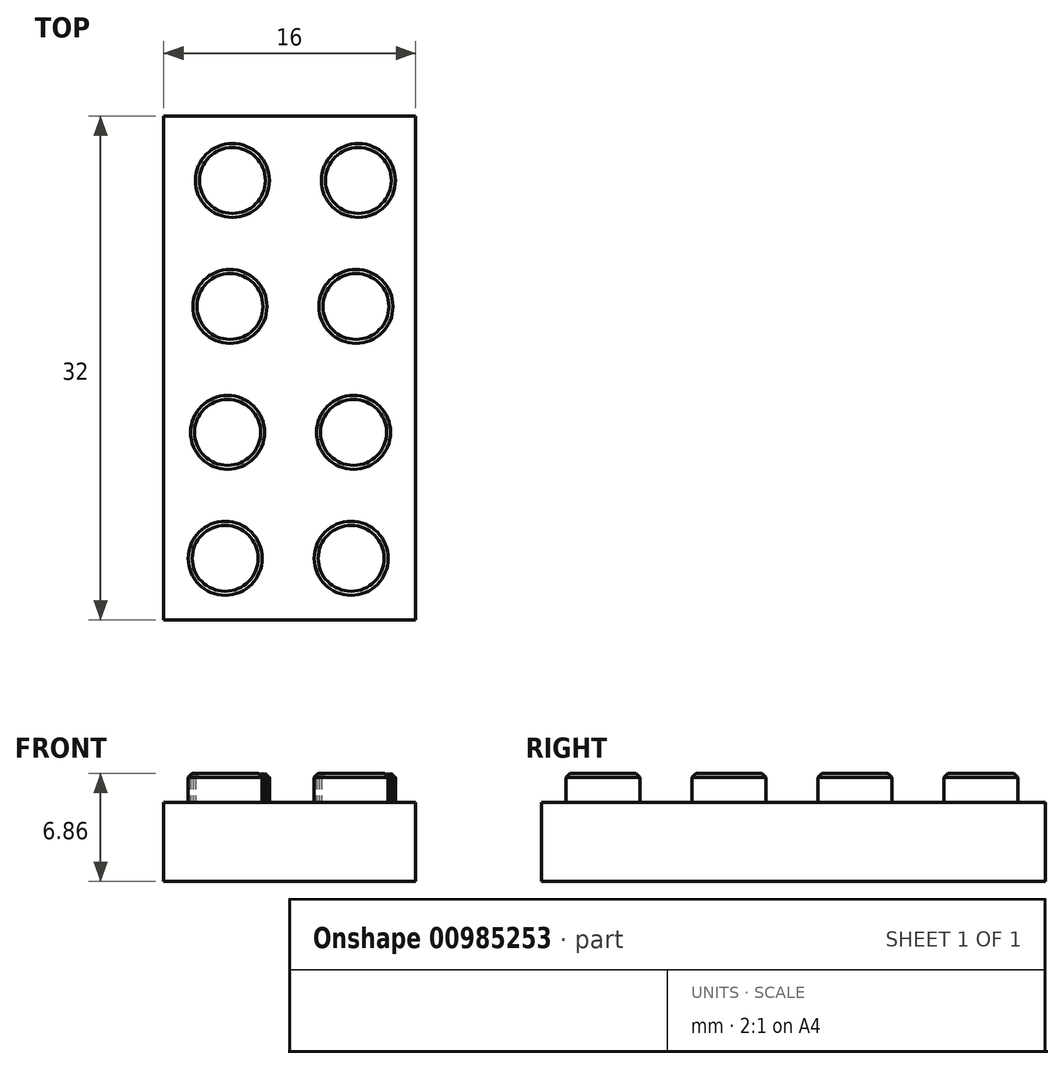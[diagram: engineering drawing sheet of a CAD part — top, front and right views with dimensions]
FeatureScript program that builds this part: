
annotation { "Feature Type Name" : "Feature", "Feature Type Description" : "" }
export const myFeature = defineFeature(function(context is Context, id is Id, definition is map)
    precondition{}
    {
        {
            var Q0;
            Q0=qCreatedBy(makeId("Top.planeOp"),FACE);
            var sketch = newSketch(context, id + "F0", { "sketchPlane" : qUnion([Q0])});
            skLineSegment(sketch, "E0.bottom", {"start": v(0, 0) * mm, "end": v(-16, 0) * mm});
            skLineSegment(sketch, "E0.top", {"start": v(0, 32) * mm, "end": v(-16, 32) * mm});
            skLineSegment(sketch, "E0.left", {"start": v(0, 0) * mm, "end": v(0, 32) * mm});
            skLineSegment(sketch, "E0.right", {"start": v(-16, 0) * mm, "end": v(-16, 32) * mm});
            skSolve(sketch);
        }
        {
            var Q0;
            Q0=makeQuery(id+"F0.imprint","IMPRINT",FACE,{"disambiguationData":[TD([[makeQuery(id+"F0.imprint","IMPRINT",EDGE,{"derivedFrom":sQuery(id+"F0.wireOp",EDGE,"E0.bottom")}),-1.0]])]});
            extrude(context, id + "F1", {"entities" : qUnion([Q0]), "depth" : 5 * mm, "offsetDistance" : 25.4 * mm});
        }
        {
            var Q0;
            Q0=makeQuery(id+"F1.opExtrude","CAP_FACE",FACE,{"disambiguationData":[OSD([sQuery(id+"F0.wireOp",EDGE,"E0.bottom"),sQuery(id+"F0.wireOp",EDGE,"E0.top"),sQuery(id+"F0.wireOp",EDGE,"E0.left"),sQuery(id+"F0.wireOp",EDGE,"E0.right")])],"isStart":false});
            var sketch = newSketch(context, id + "F2", { "sketchPlane" : qUnion([Q0])});
            skCircle(sketch, "E1", {"center": v(-12.1, 3.91) * mm, "radius": 2.35 * mm});
            skCircle(sketch, "E2.1.0.0", {"center": v(-11.94, 11.91) * mm, "radius": 2.35 * mm});
            skCircle(sketch, "E2.2.0.0", {"center": v(-11.79, 19.91) * mm, "radius": 2.35 * mm});
            skLineSegment(sketch, "E2.direction1", {"start": v(-12.1, 3.91) * mm, "end": v(-11.94, 11.91) * mm, "construction": true});
            skCircle(sketch, "E3.0.3.0", {"center": v(-11.63, 27.91) * mm, "radius": 2.35 * mm});
            skCircle(sketch, "E4.1.0.0", {"center": v(-3.63, 27.91) * mm, "radius": 2.35 * mm});
            skCircle(sketch, "E4.1.0.1", {"center": v(-3.79, 19.91) * mm, "radius": 2.35 * mm});
            skCircle(sketch, "E4.1.0.2", {"center": v(-3.94, 11.91) * mm, "radius": 2.35 * mm});
            skCircle(sketch, "E4.1.0.3", {"center": v(-4.09, 3.91) * mm, "radius": 2.35 * mm});
            skLineSegment(sketch, "E4.direction1", {"start": v(-12.1, 3.91) * mm, "end": v(-4.09, 3.91) * mm, "construction": true});
            skSolve(sketch);
        }
        {
            var Q0;
            Q0=makeQuery(id+"F2.imprint","IMPRINT",FACE,{"disambiguationData":[TD([[makeQuery(id+"F2.imprint","IMPRINT",EDGE,{"derivedFrom":sQuery(id+"F2.wireOp",EDGE,"E1")}),1.0]])]});
            var Q1;
            Q1=makeQuery(id+"F2.imprint","IMPRINT",FACE,{"disambiguationData":[TD([[makeQuery(id+"F2.imprint","IMPRINT",EDGE,{"derivedFrom":sQuery(id+"F2.wireOp",EDGE,"E2.1.0.0")}),1.0]])]});
            var Q2;
            Q2=makeQuery(id+"F2.imprint","IMPRINT",FACE,{"disambiguationData":[TD([[makeQuery(id+"F2.imprint","IMPRINT",EDGE,{"derivedFrom":sQuery(id+"F2.wireOp",EDGE,"E3.0.3.0")}),1.0]])]});
            var Q3;
            Q3=makeQuery(id+"F2.imprint","IMPRINT",FACE,{"disambiguationData":[TD([[makeQuery(id+"F2.imprint","IMPRINT",EDGE,{"derivedFrom":sQuery(id+"F2.wireOp",EDGE,"E4.1.0.3")}),1.0]])]});
            var Q4;
            Q4=makeQuery(id+"F2.imprint","IMPRINT",FACE,{"disambiguationData":[TD([[makeQuery(id+"F2.imprint","IMPRINT",EDGE,{"derivedFrom":sQuery(id+"F2.wireOp",EDGE,"E4.1.0.2")}),1.0]])]});
            var Q5;
            Q5=makeQuery(id+"F2.imprint","IMPRINT",FACE,{"disambiguationData":[TD([[makeQuery(id+"F2.imprint","IMPRINT",EDGE,{"derivedFrom":sQuery(id+"F2.wireOp",EDGE,"E4.1.0.1")}),1.0]])]});
            var Q6;
            Q6=makeQuery(id+"F2.imprint","IMPRINT",FACE,{"disambiguationData":[TD([[makeQuery(id+"F2.imprint","IMPRINT",EDGE,{"derivedFrom":sQuery(id+"F2.wireOp",EDGE,"E2.2.0.0")}),1.0]])]});
            var Q7;
            Q7=makeQuery(id+"F2.imprint","IMPRINT",FACE,{"disambiguationData":[TD([[makeQuery(id+"F2.imprint","IMPRINT",EDGE,{"derivedFrom":sQuery(id+"F2.wireOp",EDGE,"E4.1.0.0")}),1.0]])]});
            extrude(context, id + "F3", {"entities" : qUnion([Q0, Q1, Q2, Q3, Q4, Q5, Q6, Q7]), "operationType" : NewBodyOperationType.ADD, "depth" : 1.85 * mm, "offsetDistance" : 25.4 * mm});
        }
        {
            var Q0;
            Q0=makeQuery(id+"F3.opExtrude","CAP_EDGE",EDGE,{"disambiguationData":[OSD([sQuery(id+"F2.wireOp",EDGE,"E1")])],"isStart":false});
            var Q1;
            Q1=makeQuery(id+"F3.opExtrude","CAP_EDGE",EDGE,{"disambiguationData":[OSD([sQuery(id+"F2.wireOp",EDGE,"E2.1.0.0")])],"isStart":false});
            var Q2;
            Q2=makeQuery(id+"F3.opExtrude","CAP_EDGE",EDGE,{"disambiguationData":[OSD([sQuery(id+"F2.wireOp",EDGE,"E2.2.0.0")])],"isStart":false});
            var Q3;
            Q3=makeQuery(id+"F3.opExtrude","CAP_EDGE",EDGE,{"disambiguationData":[OSD([sQuery(id+"F2.wireOp",EDGE,"E3.0.3.0")])],"isStart":false});
            var Q4;
            Q4=makeQuery(id+"F3.opExtrude","CAP_EDGE",EDGE,{"disambiguationData":[OSD([sQuery(id+"F2.wireOp",EDGE,"E4.1.0.0")])],"isStart":false});
            var Q5;
            Q5=makeQuery(id+"F3.opExtrude","CAP_EDGE",EDGE,{"disambiguationData":[OSD([sQuery(id+"F2.wireOp",EDGE,"E4.1.0.1")])],"isStart":false});
            var Q6;
            Q6=makeQuery(id+"F3.opExtrude","CAP_EDGE",EDGE,{"disambiguationData":[OSD([sQuery(id+"F2.wireOp",EDGE,"E4.1.0.2")])],"isStart":false});
            var Q7;
            Q7=makeQuery(id+"F3.opExtrude","CAP_EDGE",EDGE,{"disambiguationData":[OSD([sQuery(id+"F2.wireOp",EDGE,"E4.1.0.3")])],"isStart":false});
            chamfer(context, id + "F4", {"entities" : qUnion([Q0, Q1, Q2, Q3, Q4, Q5, Q6, Q7]), "width" : 0.25 * mm, "tangentPropagation" : true});
        }
    });
